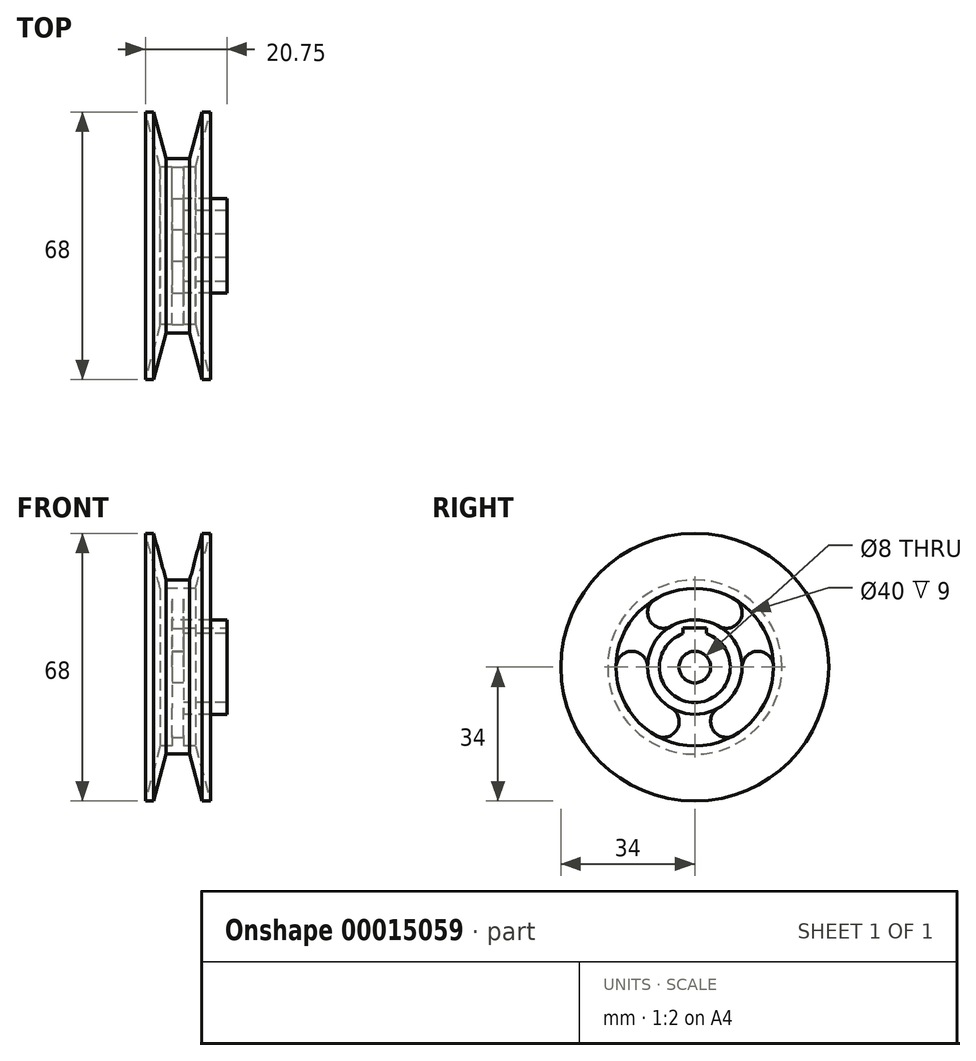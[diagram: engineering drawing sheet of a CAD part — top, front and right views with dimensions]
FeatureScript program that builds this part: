
annotation { "Feature Type Name" : "Feature", "Feature Type Description" : "" }
export const myFeature = defineFeature(function(context is Context, id is Id, definition is map)
    precondition{}
    {
        {
            var Q0;
            Q0=qCreatedBy(makeId("Front.planeOp"),FACE);
            var sketch = newSketch(context, id + "F0", { "sketchPlane" : qUnion([Q0])});
            skLineSegment(sketch, "E0", {"start": v(0, 0) * mm, "end": v(0, 13.33) * mm, "construction": true});
            skLineSegment(sketch, "E1", {"start": v(0, 0) * mm, "end": v(7.77, 0) * mm, "construction": true});
            skLineSegment(sketch, "E2.left", {"start": v(0, 0) * mm, "end": v(0, 20) * mm, "construction": true});
            skLineSegment(sketch, "E2.right", {"start": v(1.5, 4) * mm, "end": v(1.5, 9) * mm});
            skLineSegment(sketch, "E3.bottom", {"start": v(1.5, 9) * mm, "end": v(12.5, 9) * mm});
            skLineSegment(sketch, "E3.top", {"start": v(1.5, 12) * mm, "end": v(12.5, 12) * mm});
            skLineSegment(sketch, "E3.right", {"start": v(12.5, 9) * mm, "end": v(12.5, 12) * mm});
            skLineSegment(sketch, "E4.bottom", {"start": v(1.5, 20) * mm, "end": v(4.5, 20) * mm});
            skLineSegment(sketch, "E4.top", {"start": v(0, 22.13) * mm, "end": v(3, 22.13) * mm});
            skLineSegment(sketch, "E4.left", {"start": v(0, 20) * mm, "end": v(0, 22.13) * mm});
            skLineSegment(sketch, "E5", {"start": v(4.5, 20) * mm, "end": v(8.25, 34) * mm});
            skLineSegment(sketch, "E6", {"start": v(8.25, 34) * mm, "end": v(6.18, 34) * mm});
            skLineSegment(sketch, "E7", {"start": v(6.18, 34) * mm, "end": v(3, 22.13) * mm});
            skLineSegment(sketch, "E8.trimOffspring", {"start": v(1.5, 12) * mm, "end": v(1.5, 20) * mm});
            skLineSegment(sketch, "E9.0.MirrorCS", {"start": v(0, 22.13) * mm, "end": v(-3, 22.13) * mm});
            skLineSegment(sketch, "E10.0.MirrorCS", {"start": v(-6.18, 34) * mm, "end": v(-3, 22.13) * mm});
            skLineSegment(sketch, "E11.0.MirrorCS", {"start": v(-8.25, 34) * mm, "end": v(-6.18, 34) * mm});
            skLineSegment(sketch, "E12.0.MirrorCS", {"start": v(-4.5, 20) * mm, "end": v(-8.25, 34) * mm});
            skLineSegment(sketch, "E13.0.MirrorCS", {"start": v(-1.5, 12) * mm, "end": v(-1.5, 20) * mm});
            skLineSegment(sketch, "E14.0.MirrorCS", {"start": v(-1.5, 4) * mm, "end": v(-1.5, 9) * mm});
            skLineSegment(sketch, "E15.0.MirrorCS", {"start": v(-1.5, 20) * mm, "end": v(-4.5, 20) * mm});
            skLineSegment(sketch, "E16", {"start": v(-1.5, 12) * mm, "end": v(-1.5, 9) * mm});
            skLineSegment(sketch, "E17", {"start": v(-1.5, 4) * mm, "end": v(1.5, 4) * mm});
            skPoint(sketch, "E2.bottom.end.orphan", {"position": v(1.5, 0) * mm});
            skSolve(sketch);
        }
        {
            var Q0;
            Q0=makeQuery(id+"F0.imprint","IMPRINT",FACE,{"disambiguationData":[TD([[makeQuery(id+"F0.imprint","IMPRINT",EDGE,{"derivedFrom":sQuery(id+"F0.wireOp",EDGE,"E2.right")}),1.0]])]});
            var Q1;
            Q1=sQuery(id+"F0.wireOp",EDGE,"E1");
            revolve(context, id + "F1", {"entities" : qUnion([Q0]), "axis" : qUnion([Q1]), "revolveType" : RevolveType.FULL});
        }
        {
            var Q0;
            Q0=makeQuery(id+"F1.opRevolve","SWEPT_FACE",FACE,{"disambiguationData":[OSD([sQuery(id+"F0.wireOp",EDGE,"E3.right")])]});
            var sketch = newSketch(context, id + "F2", { "sketchPlane" : qUnion([Q0])});
            skArc(sketch, "E18.0", {"start": v(-3, 8.49) * mm, "mid": v(0, -9) * mm, "end": v(3, 8.49) * mm});
            skLineSegment(sketch, "E19", {"start": v(0, 0) * mm, "end": v(0, 36.47) * mm, "construction": true});
            skLineSegment(sketch, "E20.rect.bottom", {"start": v(3, 8) * mm, "end": v(-3, 8) * mm});
            skLineSegment(sketch, "E20.rect.top", {"start": v(3, 10) * mm, "end": v(-3, 10) * mm});
            skLineSegment(sketch, "E20.rect.left", {"start": v(3, 8) * mm, "end": v(3, 10) * mm});
            skLineSegment(sketch, "E20.rect.right", {"start": v(-3, 8) * mm, "end": v(-3, 10) * mm});
            skPoint(sketch, "E20.rect.middle", {"position": v(0, 9) * mm});
            skSolve(sketch);
        }
        {
            var Q0;
            {var subQ6=sQuery(id+"F2.wireOp",EDGE,"E20.rect.top");Q0=makeQuery(id+"F2.imprint","IMPRINT",FACE,{"disambiguationData":[TD([[makeQuery(id+"F2.imprint","IMPRINT",EDGE,{"derivedFrom":subQ6}),1.0]])]});}
            var Q1;
            {var subQ6=sQuery(id+"F2.wireOp",EDGE,"E20.rect.bottom");Q1=makeQuery(id+"F2.imprint","IMPRINT",FACE,{"disambiguationData":[TD([[makeQuery(id+"F2.imprint","IMPRINT",EDGE,{"derivedFrom":subQ6}),-1.0]])]});}
            var Q2;
            Q2=makeQuery(id+"F1.opRevolve","SWEPT_FACE",FACE,{"disambiguationData":[OSD([sQuery(id+"F0.wireOp",EDGE,"E2.right")])]});
            extrude(context, id + "F3", {"entities" : qUnion([Q0, Q1]), "operationType" : NewBodyOperationType.REMOVE, "endBound" : BoundingType.UP_TO_SURFACE, "oppositeDirection" : true, "endBoundEntityFace" : qUnion([Q2]), "depth" : 25 * mm});
        }
        {
            var Q0;
            Q0=makeQuery(id+"F1.opRevolve","SWEPT_FACE",FACE,{"disambiguationData":[OSD([sQuery(id+"F0.wireOp",EDGE,"E8.trimOffspring")])]});
            var sketch = newSketch(context, id + "F4", { "sketchPlane" : qUnion([Q0])});
            skLineSegment(sketch, "E21", {"start": v(0, 0) * mm, "end": v(0, 40.86) * mm, "construction": true});
            skLineSegment(sketch, "E22", {"start": v(0, 0) * mm, "end": v(19.76, 34.23) * mm, "construction": true});
            skLineSegment(sketch, "E23", {"start": v(0, 0) * mm, "end": v(-19.76, 34.23) * mm, "construction": true});
            skArc(sketch, "E24", {"start": v(11.19, 11.44) * mm, "mid": v(0, 16) * mm, "end": v(-11.19, 11.44) * mm, "construction": true});
            skArc(sketch, "E25", {"start": v(10, 17.32) * mm, "mid": v(0, 20) * mm, "end": v(-10, 17.32) * mm});
            skArc(sketch, "E26", {"start": v(6, 10.4) * mm, "mid": v(0, 12) * mm, "end": v(-6, 10.4) * mm});
            skArc(sketch, "E27", {"start": v(6, 10.4) * mm, "mid": v(11.46, 11.86) * mm, "end": v(10, 17.32) * mm});
            skArc(sketch, "E28", {"start": v(-10, 17.32) * mm, "mid": v(-11.46, 11.86) * mm, "end": v(-6, 10.4) * mm});
            skArc(sketch, "E29.1.0", {"start": v(-10, -17.32) * mm, "mid": v(-4.54, -15.86) * mm, "end": v(-6, -10.4) * mm});
            skArc(sketch, "E29.1.1", {"start": v(-12, 0) * mm, "mid": v(-16, 4) * mm, "end": v(-20, 0) * mm});
            skArc(sketch, "E29.1.2", {"start": v(-12, 0) * mm, "mid": v(-10.4, -6) * mm, "end": v(-6, -10.4) * mm});
            skArc(sketch, "E29.1.3", {"start": v(-20, 0) * mm, "mid": v(-17.32, -10) * mm, "end": v(-10, -17.32) * mm});
            skArc(sketch, "E29.2.0", {"start": v(20, 0) * mm, "mid": v(16, 4) * mm, "end": v(12, 0) * mm});
            skArc(sketch, "E29.2.1", {"start": v(6, -10.4) * mm, "mid": v(4.54, -15.86) * mm, "end": v(10, -17.32) * mm});
            skArc(sketch, "E29.2.2", {"start": v(6, -10.4) * mm, "mid": v(10.4, -6) * mm, "end": v(12, 0) * mm});
            skArc(sketch, "E29.2.3", {"start": v(10, -17.32) * mm, "mid": v(17.32, -10) * mm, "end": v(20, 0) * mm});
            skSolve(sketch);
        }
        {
            var Q0;
            Q0=makeQuery(id+"F4.imprint","IMPRINT",FACE,{"disambiguationData":[TD([[makeQuery(id+"F4.imprint","IMPRINT",EDGE,{"derivedFrom":sQuery(id+"F4.wireOp",EDGE,"E25")}),-1.0]])]});
            var Q1;
            Q1=makeQuery(id+"F4.imprint","IMPRINT",FACE,{"disambiguationData":[TD([[makeQuery(id+"F4.imprint","IMPRINT",EDGE,{"derivedFrom":sQuery(id+"F4.wireOp",EDGE,"E29.1.0")}),1.0]])]});
            var Q2;
            Q2=makeQuery(id+"F4.imprint","IMPRINT",FACE,{"disambiguationData":[TD([[makeQuery(id+"F4.imprint","IMPRINT",EDGE,{"derivedFrom":sQuery(id+"F4.wireOp",EDGE,"E29.2.0")}),1.0]])]});
            extrude(context, id + "F5", {"entities" : qUnion([Q0, Q1, Q2]), "operationType" : NewBodyOperationType.REMOVE, "endBound" : BoundingType.THROUGH_ALL, "oppositeDirection" : true, "depth" : 25 * mm});
        }
    });
